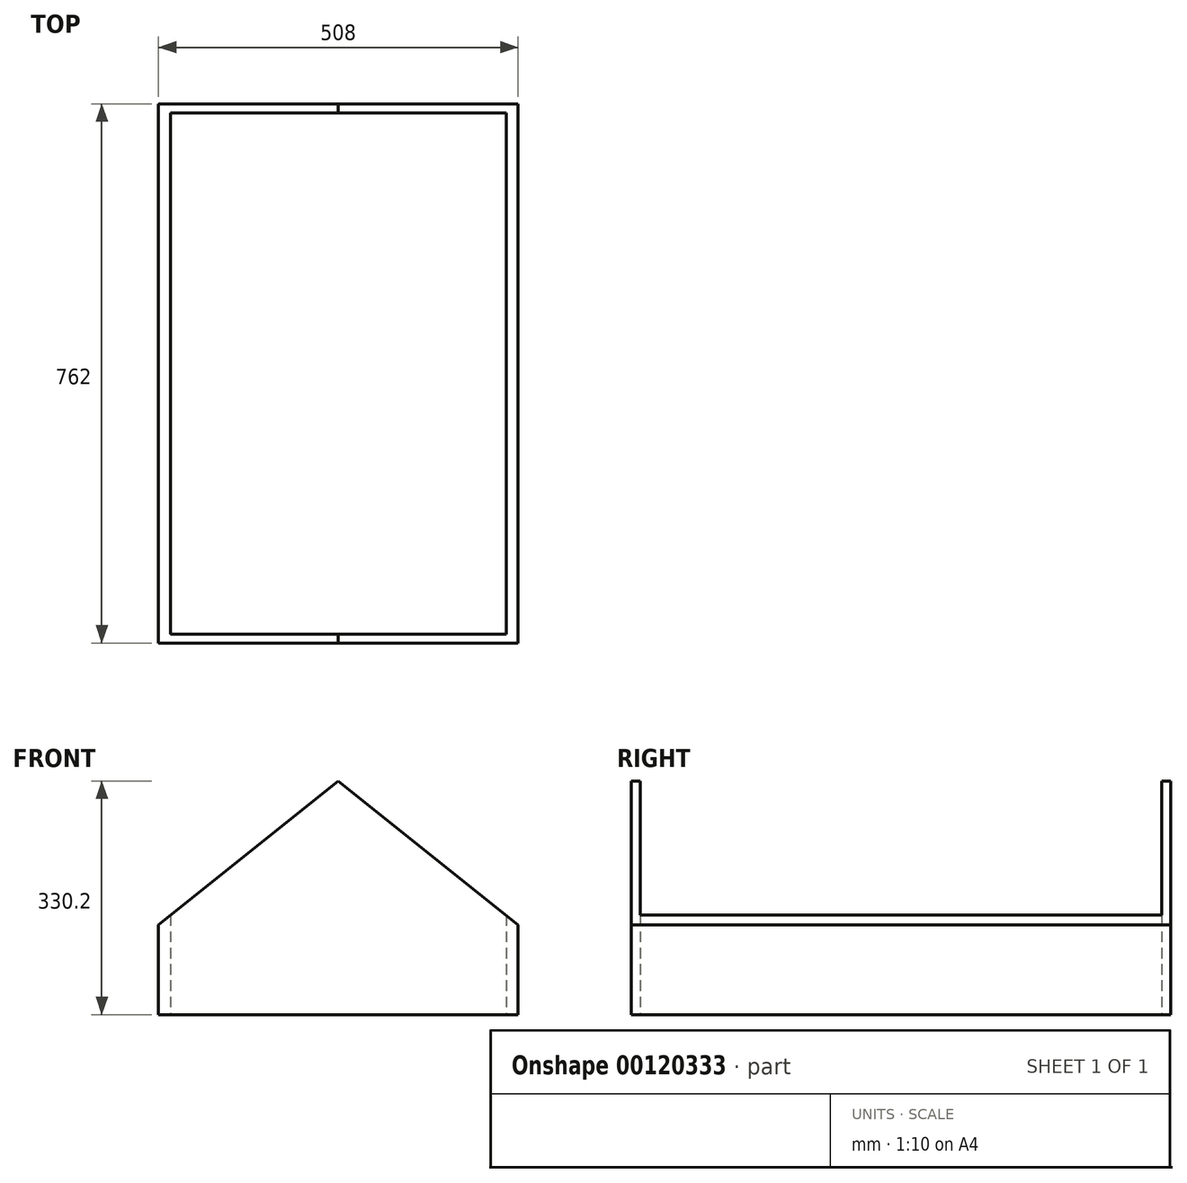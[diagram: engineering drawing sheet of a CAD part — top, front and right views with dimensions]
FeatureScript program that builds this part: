
annotation { "Feature Type Name" : "Feature", "Feature Type Description" : "" }
export const myFeature = defineFeature(function(context is Context, id is Id, definition is map)
    precondition{}
    {
        {
            var Q0;
            Q0=qCreatedBy(makeId("Top.planeOp"),FACE);
            var sketch = newSketch(context, id + "F0", { "sketchPlane" : qUnion([Q0])});
            skLineSegment(sketch, "E0.bottom", {"start": v(0, 0) * mm, "end": v(508, 0) * mm});
            skLineSegment(sketch, "E0.top", {"start": v(0, 762) * mm, "end": v(508, 762) * mm});
            skLineSegment(sketch, "E0.left", {"start": v(0, 0) * mm, "end": v(0, 762) * mm});
            skLineSegment(sketch, "E0.right", {"start": v(508, 0) * mm, "end": v(508, 762) * mm});
            skLineSegment(sketch, "E1.bottom", {"start": v(16.76, 12.7) * mm, "end": v(491.24, 12.7) * mm});
            skLineSegment(sketch, "E1.top", {"start": v(16.76, 749.3) * mm, "end": v(491.24, 749.3) * mm});
            skLineSegment(sketch, "E1.left", {"start": v(16.76, 12.7) * mm, "end": v(16.76, 749.3) * mm});
            skLineSegment(sketch, "E1.right", {"start": v(491.24, 12.7) * mm, "end": v(491.24, 749.3) * mm});
            skSolve(sketch);
        }
        {
            var Q0;
            Q0=makeQuery(id+"F0.imprint","IMPRINT",FACE,{"disambiguationData":[TD([[makeQuery(id+"F0.imprint","IMPRINT",EDGE,{"derivedFrom":sQuery(id+"F0.wireOp",EDGE,"E0.bottom")}),1.0]])]});
            extrude(context, id + "F1", {"entities" : qUnion([Q0]), "depth" : 330.2 * mm});
        }
        {
            var Q0;
            Q0=qCreatedBy(makeId("Front.planeOp"),FACE);
            var sketch = newSketch(context, id + "F2", { "sketchPlane" : qUnion([Q0])});
            skLineSegment(sketch, "E2", {"start": v(0, 127) * mm, "end": v(254, 330.2) * mm});
            skLineSegment(sketch, "E3", {"start": v(0, 330.2) * mm, "end": v(0, 127) * mm});
            skLineSegment(sketch, "E4", {"start": v(254, 0) * mm, "end": v(254, 330.2) * mm, "construction": true});
            skLineSegment(sketch, "E5.MirrorCS", {"start": v(508, 127) * mm, "end": v(254, 330.2) * mm});
            skLineSegment(sketch, "E6.MirrorCS", {"start": v(508, 330.2) * mm, "end": v(508, 127) * mm});
            skLineSegment(sketch, "E7.MirrorCS", {"start": v(254, 330.2) * mm, "end": v(508, 330.2) * mm});
            skLineSegment(sketch, "E8", {"start": v(0, 330.2) * mm, "end": v(254, 330.2) * mm});
            skSolve(sketch);
        }
        {
            var Q0;
            Q0 = qSketchRegion(id + "F2", true);
            extrude(context, id + "F3", {"entities" : qUnion([Q0]), "operationType" : NewBodyOperationType.REMOVE, "endBound" : BoundingType.THROUGH_ALL, "oppositeDirection" : true, "depth" : 25.4 * mm});
        }
    });
